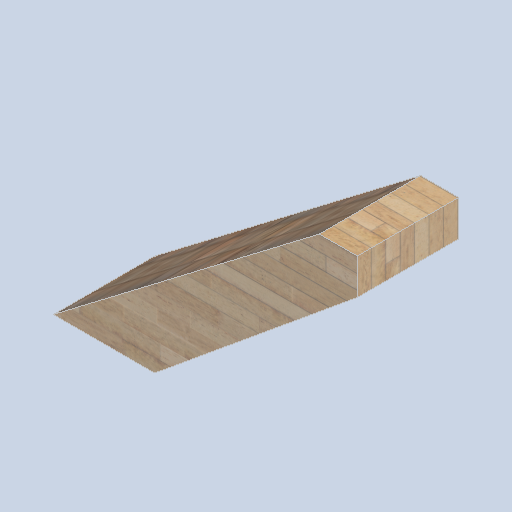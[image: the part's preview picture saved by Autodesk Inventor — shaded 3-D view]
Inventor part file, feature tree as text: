
AUTODESK INVENTOR PART (.ipt)
format: ipt  version: 2024.2 (Build 282272000, 272)  size: 161,280 bytes
history: native  units: in
note: dims shown in document units (in); Inventor stores cm internally (conversion verified against a paired STEP export)
features: other x3, sketch x1
ambient origin geometry x8: Origin, YZ Plane, XZ Plane, XY Plane, X Axis, Y Axis, Z Axis, Center Point
bodies: Body1 (feature_tree)
feature tree (4):
  other  "frame_rib_02.ipt"
  other  "Solid3::frame_rib_02.ipt"
  other  "TaggingFeature1"
  sketch  "Sketch1"  dims[d0=0.3937in]
